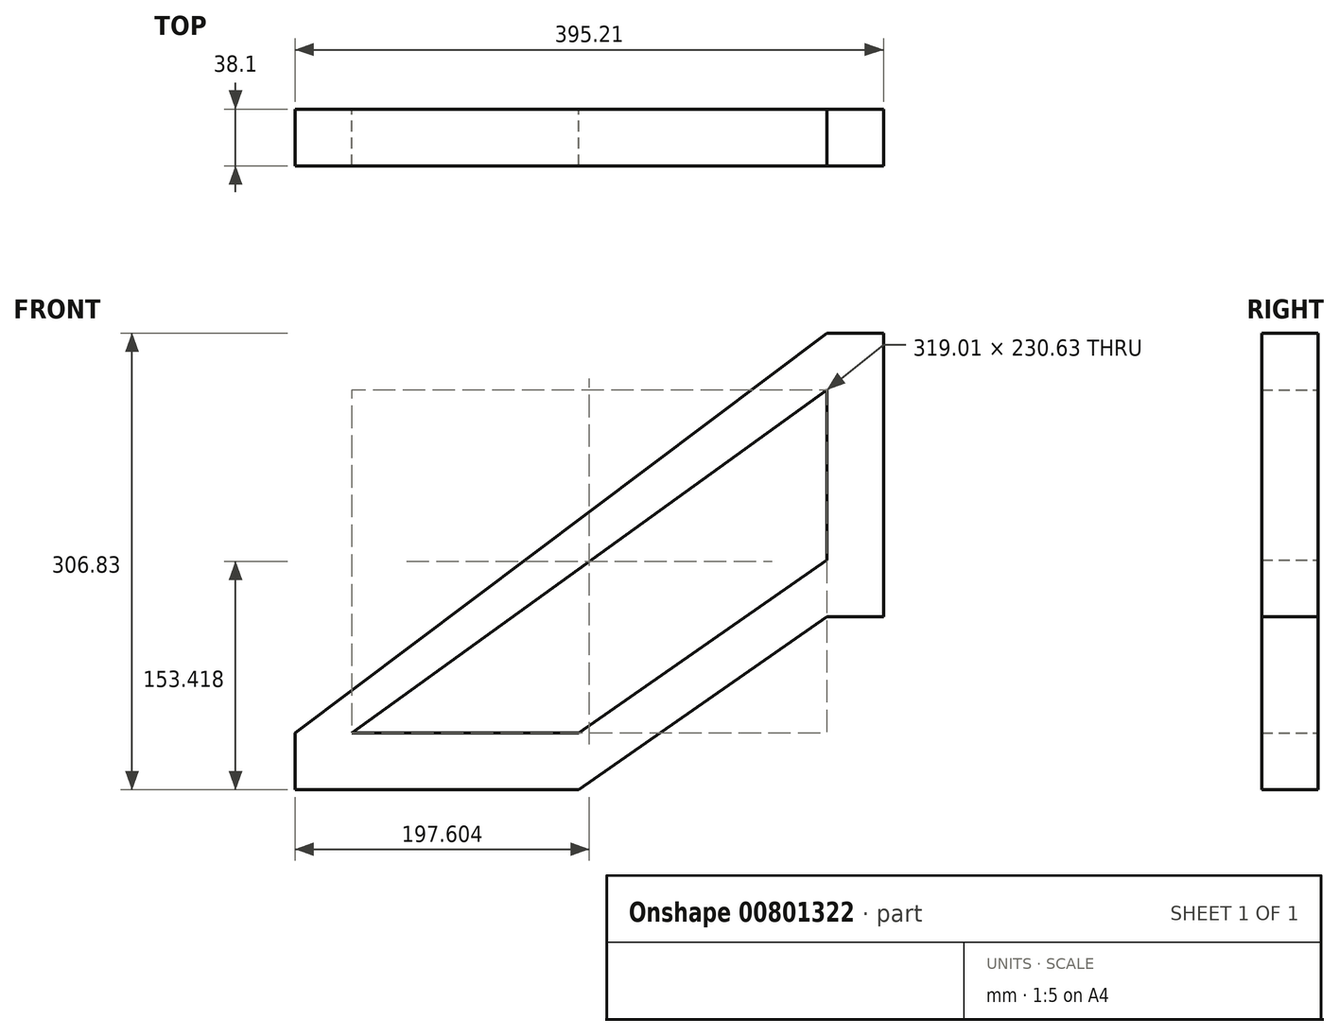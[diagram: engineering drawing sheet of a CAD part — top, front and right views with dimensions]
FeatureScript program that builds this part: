
annotation { "Feature Type Name" : "Feature", "Feature Type Description" : "" }
export const myFeature = defineFeature(function(context is Context, id is Id, definition is map)
    precondition{}
    {
        {
            var Q0;
            Q0=qCreatedBy(makeId("Front.planeOp"),FACE);
            var sketch = newSketch(context, id + "F0", { "sketchPlane" : qUnion([Q0])});
            skLineSegment(sketch, "E0", {"start": v(-152.4, -6.57) * mm, "end": v(0, -6.57) * mm});
            skLineSegment(sketch, "E1", {"start": v(0, -6.57) * mm, "end": v(0, 31.53) * mm});
            skLineSegment(sketch, "E2", {"start": v(0, 31.53) * mm, "end": v(-152.4, 31.53) * mm});
            skLineSegment(sketch, "E3", {"start": v(-152.4, 31.53) * mm, "end": v(-152.4, -6.57) * mm});
            skLineSegment(sketch, "E4", {"start": v(0, 31.53) * mm, "end": v(166.6, 147.86) * mm});
            skLineSegment(sketch, "E5", {"start": v(166.6, 147.86) * mm, "end": v(166.6, 109.76) * mm});
            skLineSegment(sketch, "E6", {"start": v(166.6, 109.76) * mm, "end": v(0, -6.57) * mm});
            skLineSegment(sketch, "E7", {"start": v(166.6, 109.76) * mm, "end": v(204.7, 109.76) * mm});
            skLineSegment(sketch, "E8", {"start": v(204.7, 109.76) * mm, "end": v(204.7, 262.16) * mm});
            skLineSegment(sketch, "E9", {"start": v(204.7, 262.16) * mm, "end": v(166.6, 262.16) * mm});
            skLineSegment(sketch, "E10", {"start": v(166.6, 262.16) * mm, "end": v(166.6, 147.86) * mm});
            skLineSegment(sketch, "E11", {"start": v(-152.4, 31.53) * mm, "end": v(-190.5, 31.53) * mm});
            skLineSegment(sketch, "E12", {"start": v(-190.5, 31.53) * mm, "end": v(-190.5, -6.57) * mm});
            skLineSegment(sketch, "E13", {"start": v(-190.5, -6.57) * mm, "end": v(-152.4, -6.57) * mm});
            skLineSegment(sketch, "E14", {"start": v(166.6, 262.16) * mm, "end": v(166.6, 300.26) * mm});
            skLineSegment(sketch, "E15", {"start": v(166.6, 300.26) * mm, "end": v(204.7, 300.26) * mm});
            skLineSegment(sketch, "E16", {"start": v(204.7, 300.26) * mm, "end": v(204.7, 262.16) * mm});
            skLineSegment(sketch, "E17", {"start": v(166.6, 300.26) * mm, "end": v(-190.5, 31.53) * mm});
            skLineSegment(sketch, "E18", {"start": v(-152.4, 31.53) * mm, "end": v(166.6, 262.16) * mm});
            skSolve(sketch);
        }
        {
            var Q0;
            Q0=makeQuery(id+"F0.imprint","IMPRINT",FACE,{"disambiguationData":[TD([[makeQuery(id+"F0.imprint","IMPRINT",EDGE,{"derivedFrom":sQuery(id+"F0.wireOp",EDGE,"E11")}),-1.0]])]});
            extrude(context, id + "F1", {"entities" : qUnion([Q0]), "depth" : 38.1 * mm, "offsetDistance" : 25.4 * mm});
        }
        {
            var Q0;
            Q0 = qSketchRegion(id + "F0", true);
            extrude(context, id + "F2", {"entities" : qUnion([Q0]), "operationType" : NewBodyOperationType.ADD, "depth" : 38.1 * mm, "offsetDistance" : 25.4 * mm});
        }
    });
